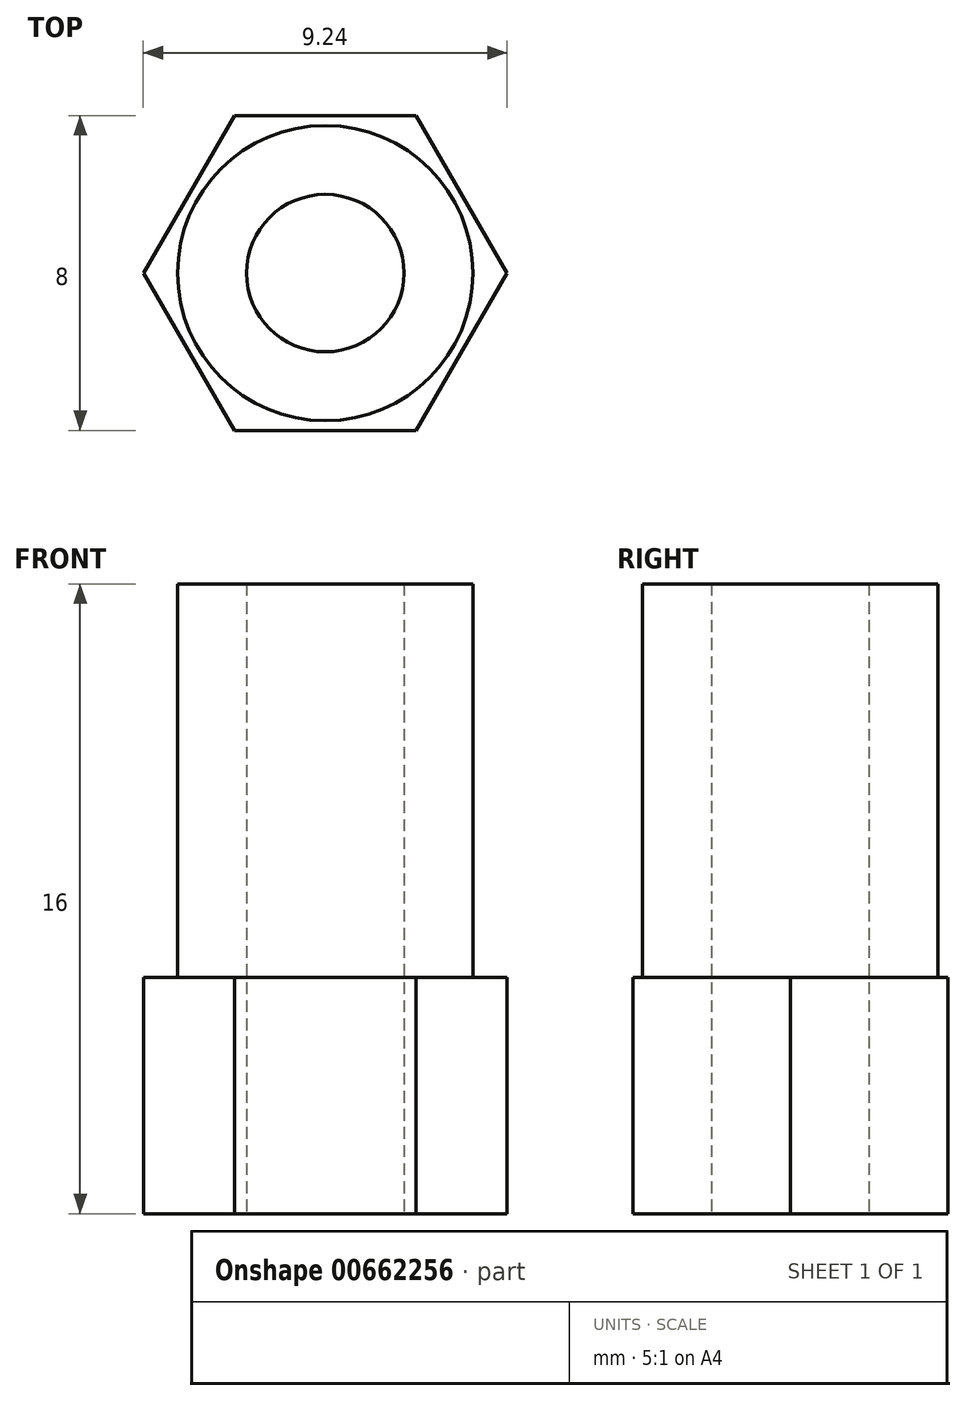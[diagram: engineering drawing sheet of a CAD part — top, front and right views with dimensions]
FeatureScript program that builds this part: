
annotation { "Feature Type Name" : "Feature", "Feature Type Description" : "" }
export const myFeature = defineFeature(function(context is Context, id is Id, definition is map)
    precondition{}
    {
        {
            var Q0;
            Q0=qCreatedBy(makeId("Top.planeOp"),FACE);
            var sketch = newSketch(context, id + "F0", { "sketchPlane" : qUnion([Q0])});
            skCircle(sketch, "E0.cCircle", {"center": v(-19.57, 5.72) * mm, "radius": 4 * mm, "construction": true});
            skLineSegment(sketch, "E0.0", {"start": v(-21.88, 9.72) * mm, "end": v(-17.26, 9.72) * mm});
            skLineSegment(sketch, "E0.1", {"start": v(-17.26, 9.72) * mm, "end": v(-14.95, 5.72) * mm});
            skLineSegment(sketch, "E0.2", {"start": v(-14.95, 5.72) * mm, "end": v(-17.26, 1.72) * mm});
            skLineSegment(sketch, "E0.3", {"start": v(-17.26, 1.72) * mm, "end": v(-21.88, 1.72) * mm});
            skLineSegment(sketch, "E0.4", {"start": v(-21.88, 1.72) * mm, "end": v(-24.19, 5.72) * mm});
            skLineSegment(sketch, "E0.5", {"start": v(-24.19, 5.72) * mm, "end": v(-21.88, 9.72) * mm});
            skPoint(sketch, "E0.0.midPoint", {"position": v(-19.57, 9.72) * mm});
            skSolve(sketch);
        }
        {
            var Q0;
            Q0 = qSketchRegion(id + "F0", true);
            extrude(context, id + "F1", {"entities" : qUnion([Q0]), "depth" : 6 * mm, "offsetDistance" : 25 * mm});
        }
        {
            var Q0;
            Q0=makeQuery(id+"F1.opExtrude","CAP_FACE",FACE,{"disambiguationData":[OSD([sQuery(id+"F0.wireOp",EDGE,"E0.0"),sQuery(id+"F0.wireOp",EDGE,"E0.1"),sQuery(id+"F0.wireOp",EDGE,"E0.2"),sQuery(id+"F0.wireOp",EDGE,"E0.3"),sQuery(id+"F0.wireOp",EDGE,"E0.4"),sQuery(id+"F0.wireOp",EDGE,"E0.5")])],"isStart":false});
            var sketch = newSketch(context, id + "F2", { "sketchPlane" : qUnion([Q0])});
            skCircle(sketch, "E1", {"center": v(-19.57, 5.72) * mm, "radius": 3.75 * mm});
            skPoint(sketch, "E1.centerSnap0", {"position": v(-19.57, 9.72) * mm});
            skSolve(sketch);
        }
        {
            var Q0;
            Q0 = qSketchRegion(id + "F2", true);
            extrude(context, id + "F3", {"entities" : qUnion([Q0]), "operationType" : NewBodyOperationType.ADD, "depth" : 10 * mm, "offsetDistance" : 25 * mm});
        }
        {
            var Q0;
            Q0=makeQuery(id+"F1.opExtrude","CAP_FACE",FACE,{"disambiguationData":[OSD([sQuery(id+"F0.wireOp",EDGE,"E0.0"),sQuery(id+"F0.wireOp",EDGE,"E0.1"),sQuery(id+"F0.wireOp",EDGE,"E0.2"),sQuery(id+"F0.wireOp",EDGE,"E0.3"),sQuery(id+"F0.wireOp",EDGE,"E0.4"),sQuery(id+"F0.wireOp",EDGE,"E0.5")])],"isStart":true});
            var sketch = newSketch(context, id + "F4", { "sketchPlane" : qUnion([Q0])});
            skCircle(sketch, "E2", {"center": v(-19.57, -5.72) * mm, "radius": 2 * mm});
            skPoint(sketch, "E2.centerSnap0", {"position": v(-19.57, -1.72) * mm});
            skPoint(sketch, "E2.perimeterSnap0", {"position": v(-19.57, -1.72) * mm});
            skPoint(sketch, "E2.perimeterSnap1", {"position": v(-16.1, -3.72) * mm});
            skSolve(sketch);
        }
        {
            var Q0;
            Q0 = qSketchRegion(id + "F4", true);
            extrude(context, id + "F5", {"entities" : qUnion([Q0]), "operationType" : NewBodyOperationType.REMOVE, "oppositeDirection" : true, "depth" : 25 * mm, "offsetDistance" : 25 * mm});
        }
    });
